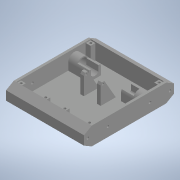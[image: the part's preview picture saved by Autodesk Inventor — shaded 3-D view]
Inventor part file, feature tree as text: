
AUTODESK INVENTOR PART (.ipt)
format: ipt  version: 2020 (Build 240168000, 168)  size: 399,872 bytes
history: native  units: in
note: dims shown in document units (in); Inventor stores cm internally (conversion verified against a paired STEP export)
features: projected_geometry x13, extrude x11, sketch x11, mirror x4, plane x1
ambient origin geometry x8: Origin, YZ Plane, XZ Plane, XY Plane, X Axis, Y Axis, Z Axis, Center Point
bodies: Solid1 (feature_tree)
feature tree (40):
  extrude  "Extrusion1"  Depth=5.9055in
  extrude  "Extrusion2"  TaperAngle=0.0deg  [1 undecoded]
  extrude  "Extrusion3"  Depth=1.063in
  extrude  "Extrusion4"  Depth=0.315in
  extrude  "Extrusion5"  TaperAngle=0.0deg  [1 undecoded]
  extrude  "Extrusion6"  Depth=0.5906in
  mirror  "Mirror1"
  extrude  "Extrusion7"  Depth=0.0787in
  mirror  "Mirror2"
  extrude  "Extrusion8"  Depth=0.5512in
  mirror  "Mirror3"
  plane  "Work Plane1"
  extrude  "Extrusion9"  Depth=0.7874in TaperAngle=0.0deg
  mirror  "Mirror4"
  extrude  "Extrusion10"  Depth=6.063in TaperAngle=0.0deg
  extrude  "Extrusion11"  Depth=0.1575in
  sketch  "Sketch1"  dims[d0=1.1811in d1=5.9055in]
  sketch  "Sketch2"  dims[d2=5.1181in d3=0.0in]
  projected_geometry  "Projected Loop1"
  sketch  "Sketch3"  dims[d4=0.1575in d5=1.063in]
  projected_geometry  "Projected Loop2"
  projected_geometry  "Projected Loop3"
  sketch  "Sketch4"  dims[d6=0.0in d8=0.315in]
  sketch  "Sketch5"  dims[d10=0.993in d11=0.0in]
  projected_geometry  "Projected Loop4"
  sketch  "Sketch6"  dims[d12=0.6496in d13=0.5906in]
  sketch  "Sketch7"  dims[d14=1.5748in d15=0.0787in]
  sketch  "Sketch9"  dims[d16=0.5512in d17=0.0in d18=0.6102in]
  sketch  "Sketch10"  dims[d19=0.4803in d20=0.7874in d21=0.0in]
  sketch  "Sketch12"  dims[d22=0.1654in d23=6.063in d24=0.0in]
  projected_geometry  "Projected Loop6"
  projected_geometry  "Projected Loop7"
  projected_geometry  "Projected Loop8"
  sketch  "Sketch13"  dims[d25=0.5114in d26=0.1575in d27=1.5748in d28=0.0in d29=0.0in d30=0.1575in d31=0.2756in d32=0.0in d33=0.4331in d34=0.122in d38=2.7559in d40=0.061in d41=0.0909in d42=0.2362in d43=0.0in d44=60.0deg d45=0.0787in d46=0.315in d48=0.993in d49=0.0in d51=0.1575in d52=0.1575in d53=0.2756in d54=0.0in d55=0.4724in]
  projected_geometry  "Projected Loop9"
  projected_geometry  "Projected Loop10"
  projected_geometry  "Projected Loop11"
  projected_geometry  "Projected Loop12"
  projected_geometry  "Projected Loop13"
  projected_geometry  "Projected Loop14"
note: 2 required parameter values undecoded (feature->parameter linkage not recoverable at this tier; creation-order binding heuristic only, values carry confidence <= 0.55)
